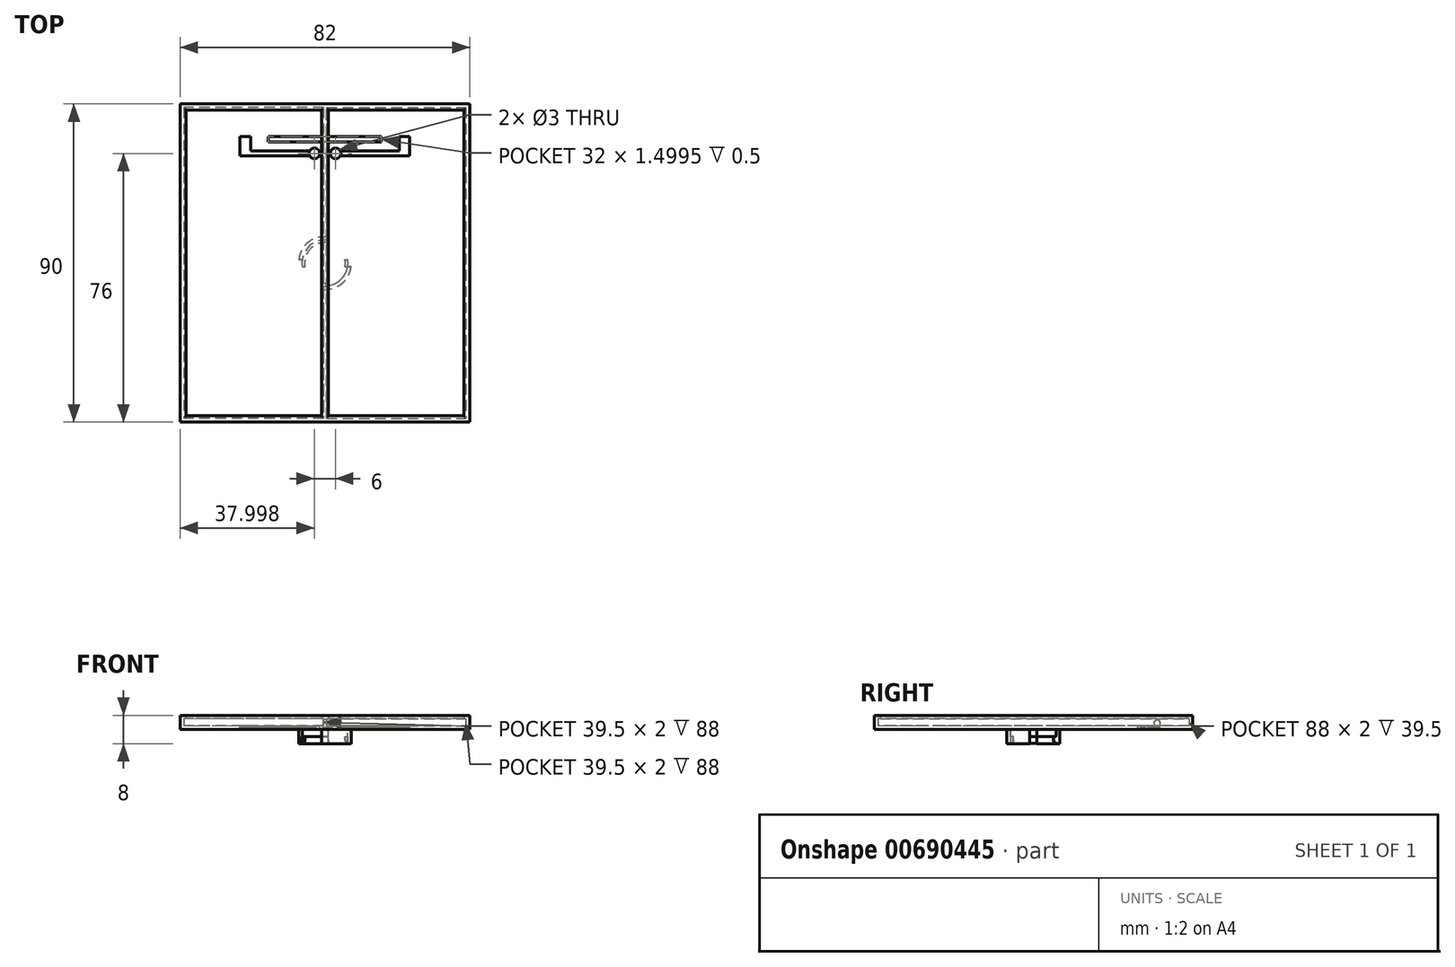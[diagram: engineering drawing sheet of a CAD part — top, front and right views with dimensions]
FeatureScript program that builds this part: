
annotation { "Feature Type Name" : "Feature", "Feature Type Description" : "" }
export const myFeature = defineFeature(function(context is Context, id is Id, definition is map)
    precondition{}
    {
        {
            var Q0;
            Q0=qCreatedBy(makeId("Top.planeOp"),FACE);
            var sketch = newSketch(context, id + "F0", { "sketchPlane" : qUnion([Q0])});
            skLineSegment(sketch, "E0.bottom", {"start": v(41, -45) * mm, "end": v(-41, -45) * mm});
            skLineSegment(sketch, "E0.top", {"start": v(41, 45) * mm, "end": v(-41, 45) * mm});
            skLineSegment(sketch, "E0.left", {"start": v(41, -45) * mm, "end": v(41, 45) * mm});
            skLineSegment(sketch, "E0.right", {"start": v(-41, -45) * mm, "end": v(-41, 45) * mm});
            skPoint(sketch, "E0.middle", {"position": v(0, 0) * mm});
            skPoint(sketch, "E1.startSnap0", {"position": v(0, 45) * mm});
            skPoint(sketch, "E1.endSnap0", {"position": v(0, -45) * mm});
            skLineSegment(sketch, "E2.top", {"start": v(1, 45) * mm, "end": v(0, 45) * mm});
            skLineSegment(sketch, "E2.left", {"start": v(1, -43.25) * mm, "end": v(1, 43.25) * mm});
            skLineSegment(sketch, "E2.right", {"start": v(-1, -43.25) * mm, "end": v(-1, 43.25) * mm});
            skLineSegment(sketch, "E3.bottom", {"start": v(39.27, -43.25) * mm, "end": v(1, -43.25) * mm});
            skLineSegment(sketch, "E3.top", {"start": v(39.27, 43.25) * mm, "end": v(1, 43.25) * mm});
            skLineSegment(sketch, "E3.left", {"start": v(39.27, -43.25) * mm, "end": v(39.27, 43.25) * mm});
            skLineSegment(sketch, "E3.right", {"start": v(-39.27, -43.25) * mm, "end": v(-39.27, 43.25) * mm});
            skLineSegment(sketch, "E4.trimOffspring", {"start": v(-1, -43.25) * mm, "end": v(-39.27, -43.25) * mm});
            skLineSegment(sketch, "E5.trimOffspring", {"start": v(-1, 43.25) * mm, "end": v(-39.27, 43.25) * mm});
            skPoint(sketch, "E6.orphan", {"position": v(-1, 45) * mm});
            skPoint(sketch, "E7.orphan", {"position": v(1, -45) * mm});
            skPoint(sketch, "E2.bottom.end.orphan", {"position": v(-1, -45) * mm});
            skLineSegment(sketch, "E8.bottom", {"start": v(-0.39, 44) * mm, "end": v(-39.89, 44) * mm});
            skLineSegment(sketch, "E8.top", {"start": v(-0.39, -44) * mm, "end": v(-39.89, -44) * mm});
            skLineSegment(sketch, "E8.left", {"start": v(-0.39, 44) * mm, "end": v(-0.39, -44) * mm});
            skLineSegment(sketch, "E8.right", {"start": v(-39.89, 44) * mm, "end": v(-39.89, -44) * mm});
            skPoint(sketch, "E8.middle", {"position": v(-20.14, 0) * mm});
            skLineSegment(sketch, "E9", {"start": v(0, -54.1) * mm, "end": v(0, 63.67) * mm, "construction": true});
            skLineSegment(sketch, "E10.MirrorCS", {"start": v(0.39, -44) * mm, "end": v(39.89, -44) * mm});
            skLineSegment(sketch, "E11.MirrorCS", {"start": v(0.39, 44) * mm, "end": v(0.39, -44) * mm});
            skLineSegment(sketch, "E12.MirrorCS", {"start": v(0.39, 44) * mm, "end": v(39.89, 44) * mm});
            skLineSegment(sketch, "E13.MirrorCS", {"start": v(39.89, 44) * mm, "end": v(39.89, -44) * mm});
            skSolve(sketch);
        }
        {
            var Q0;
            Q0=makeQuery(id+"F0.imprint","IMPRINT",FACE,{"disambiguationData":[TD([[makeQuery(id+"F0.imprint","IMPRINT",EDGE,{"derivedFrom":sQuery(id+"F0.wireOp",EDGE,"E2.right")}),-1.0]])]});
            var Q1;
            Q1=makeQuery(id+"F0.imprint","IMPRINT",FACE,{"disambiguationData":[TD([[makeQuery(id+"F0.imprint","IMPRINT",EDGE,{"derivedFrom":sQuery(id+"F0.wireOp",EDGE,"E2.left")}),1.0]])]});
            var Q2;
            Q2=makeQuery(id+"F0.imprint","IMPRINT",FACE,{"disambiguationData":[TD([[makeQuery(id+"F0.imprint","IMPRINT",EDGE,{"derivedFrom":sQuery(id+"F0.wireOp",EDGE,"E0.bottom")}),-1.0]])]});
            extrude(context, id + "F1", {"entities" : qUnion([Q0, Q1, Q2]), "depth" : 3 * mm, "offsetDistance" : 25 * mm});
        }
        {
            var Q0;
            {var subQ5=sQuery(id+"F0.wireOp",EDGE,"E3.left");Q0=makeQuery(id+"F0.imprint","IMPRINT",FACE,{"disambiguationData":[TD([[makeQuery(id+"F0.imprint","IMPRINT",EDGE,{"derivedFrom":subQ5}),1.0]])]});}
            var Q1;
            {var subQ5=sQuery(id+"F0.wireOp",EDGE,"E3.right");Q1=makeQuery(id+"F0.imprint","IMPRINT",FACE,{"disambiguationData":[TD([[makeQuery(id+"F0.imprint","IMPRINT",EDGE,{"derivedFrom":subQ5}),-1.0]])]});}
            var Q2;
            {var subQ5=sQuery(id+"F0.wireOp",EDGE,"E0.left");Q2=makeQuery(id+"F0.imprint","IMPRINT",FACE,{"disambiguationData":[TD([[makeQuery(id+"F0.imprint","IMPRINT",EDGE,{"derivedFrom":subQ5}),1.0]])]});}
            var Q3;
            {var subQ0=sQuery(id+"F0.wireOp",EDGE,"E0.right");Q3=makeQuery(id+"F0.imprint","IMPRINT",FACE,{"disambiguationData":[TD([[makeQuery(id+"F0.imprint","IMPRINT",EDGE,{"derivedFrom":subQ0}),-1.0]])]});}
            var Q4;
            {var subQ0=sQuery(id+"F0.wireOp",EDGE,"E3.bottom");var subQ1=sQuery(id+"F0.wireOp",EDGE,"E2.left");var subQ2=makeQuery(id+"F0.imprint","INTERSECT",VERTEX,{"derivedFrom":[subQ1,subQ0]});Q4=makeQuery(id+"F0.imprint","IMPRINT",FACE,{"disambiguationData":[TD([[makeQuery(id+"F0.imprint","IMPRINT",EDGE,{"disambiguationData":[TD([[subQ2,-1.0]])],"derivedFrom":subQ1}),1.0]])]});}
            var Q5;
            {var subQ0=sQuery(id+"F0.wireOp",EDGE,"E2.top");Q5=makeQuery(id+"F0.imprint","IMPRINT",FACE,{"disambiguationData":[TD([[makeQuery(id+"F0.imprint","IMPRINT",EDGE,{"derivedFrom":subQ0}),1.0]])]});}
            var Q6;
            {var subQ0=sQuery(id+"F0.wireOp",EDGE,"E2.bottom");Q6=makeQuery(id+"F0.imprint","IMPRINT",FACE,{"disambiguationData":[TD([[makeQuery(id+"F0.imprint","IMPRINT",EDGE,{"derivedFrom":subQ0}),-1.0]])]});}
            var Q7;
            Q7=makeQuery(id+"F0.imprint","IMPRINT",FACE,{"disambiguationData":[TD([[makeQuery(id+"F0.imprint","IMPRINT",EDGE,{"derivedFrom":sQuery(id+"F0.wireOp",EDGE,"E2.right")}),-1.0]])]});
            extrude(context, id + "F2", {"entities" : qUnion([Q0, Q1, Q2, Q3, Q4, Q5, Q6, Q7]), "operationType" : NewBodyOperationType.ADD, "oppositeDirection" : true, "depth" : 1 * mm, "offsetDistance" : 25 * mm});
        }
        {
            var Q0;
            Q0=makeQuery(id+"F0.imprint","IMPRINT",FACE,{"disambiguationData":[TD([[makeQuery(id+"F0.imprint","IMPRINT",EDGE,{"derivedFrom":sQuery(id+"F0.wireOp",EDGE,"E2.right")}),-1.0]])]});
            var Q1;
            Q1=makeQuery(id+"F0.imprint","IMPRINT",FACE,{"disambiguationData":[TD([[makeQuery(id+"F0.imprint","IMPRINT",EDGE,{"derivedFrom":sQuery(id+"F0.wireOp",EDGE,"E2.left")}),1.0]])]});
            extrude(context, id + "F3", {"entities" : qUnion([Q0, Q1]), "operationType" : NewBodyOperationType.REMOVE, "depth" : 2 * mm, "offsetDistance" : 25 * mm});
        }
        {
            var Q0;
            Q0=makeQuery(id+"F3.boolean.opBoolean","COPY",EDGE,{"derivedFrom":makeQuery(id+"F3.opExtrude","CAP_EDGE",EDGE,{"disambiguationData":[OSD([sQuery(id+"F0.wireOp",EDGE,"E3.left")])],"isStart":false})});
            var Q1;
            Q1=makeQuery(id+"F1.opExtrude","CAP_EDGE",EDGE,{"disambiguationData":[OSD([sQuery(id+"F0.wireOp",EDGE,"E3.left")])],"isStart":false});
            var Q2;
            Q2=makeQuery(id+"F3.boolean.opBoolean","COPY",EDGE,{"derivedFrom":makeQuery(id+"F3.opExtrude","CAP_EDGE",EDGE,{"disambiguationData":[OSD([sQuery(id+"F0.wireOp",EDGE,"E2.right")])],"isStart":false})});
            var Q3;
            Q3=makeQuery(id+"F1.opExtrude","CAP_EDGE",EDGE,{"disambiguationData":[OSD([sQuery(id+"F0.wireOp",EDGE,"E2.right")])],"isStart":false});
            var Q4;
            Q4=makeQuery(id+"F1.opExtrude","CAP_EDGE",EDGE,{"disambiguationData":[OSD([sQuery(id+"F0.wireOp",EDGE,"E4.trimOffspring")])],"isStart":false});
            var Q5;
            Q5=makeQuery(id+"F3.boolean.opBoolean","COPY",EDGE,{"derivedFrom":makeQuery(id+"F3.opExtrude","CAP_EDGE",EDGE,{"disambiguationData":[OSD([sQuery(id+"F0.wireOp",EDGE,"E4.trimOffspring")])],"isStart":false})});
            var Q6;
            Q6=makeQuery(id+"F3.boolean.opBoolean","COPY",EDGE,{"derivedFrom":makeQuery(id+"F3.opExtrude","CAP_EDGE",EDGE,{"disambiguationData":[OSD([sQuery(id+"F0.wireOp",EDGE,"E3.bottom")])],"isStart":false})});
            var Q7;
            Q7=makeQuery(id+"F1.opExtrude","CAP_EDGE",EDGE,{"disambiguationData":[OSD([sQuery(id+"F0.wireOp",EDGE,"E3.bottom")])],"isStart":false});
            var Q8;
            Q8=makeQuery(id+"F1.opExtrude","CAP_EDGE",EDGE,{"disambiguationData":[OSD([sQuery(id+"F0.wireOp",EDGE,"E2.left")])],"isStart":false});
            var Q9;
            Q9=makeQuery(id+"F3.boolean.opBoolean","COPY",EDGE,{"derivedFrom":makeQuery(id+"F3.opExtrude","CAP_EDGE",EDGE,{"disambiguationData":[OSD([sQuery(id+"F0.wireOp",EDGE,"E2.left")])],"isStart":false})});
            var Q10;
            Q10=makeQuery(id+"F1.opExtrude","CAP_EDGE",EDGE,{"disambiguationData":[OSD([sQuery(id+"F0.wireOp",EDGE,"E3.right")])],"isStart":false});
            var Q11;
            Q11=makeQuery(id+"F3.boolean.opBoolean","COPY",EDGE,{"derivedFrom":makeQuery(id+"F3.opExtrude","CAP_EDGE",EDGE,{"disambiguationData":[OSD([sQuery(id+"F0.wireOp",EDGE,"E3.right")])],"isStart":false})});
            var Q12;
            Q12=makeQuery(id+"F1.opExtrude","CAP_EDGE",EDGE,{"disambiguationData":[OSD([sQuery(id+"F0.wireOp",EDGE,"E5.trimOffspring")])],"isStart":false});
            var Q13;
            Q13=makeQuery(id+"F3.boolean.opBoolean","COPY",EDGE,{"derivedFrom":makeQuery(id+"F3.opExtrude","CAP_EDGE",EDGE,{"disambiguationData":[OSD([sQuery(id+"F0.wireOp",EDGE,"E5.trimOffspring")])],"isStart":false})});
            var Q14;
            Q14=makeQuery(id+"F3.boolean.opBoolean","COPY",EDGE,{"derivedFrom":makeQuery(id+"F3.opExtrude","CAP_EDGE",EDGE,{"disambiguationData":[OSD([sQuery(id+"F0.wireOp",EDGE,"E3.top")])],"isStart":false})});
            var Q15;
            Q15=makeQuery(id+"F1.opExtrude","CAP_EDGE",EDGE,{"disambiguationData":[OSD([sQuery(id+"F0.wireOp",EDGE,"E3.top")])],"isStart":false});
            fillet(context, id + "F4", {"entities" : qUnion([Q0, Q1, Q2, Q3, Q4, Q5, Q6, Q7, Q8, Q9, Q10, Q11, Q12, Q13, Q14, Q15]), "radius" : 0.25 * mm, "tangentPropagation" : true, "allowEdgeOverflow" : false});
        }
        {
            var Q0;
            Q0=makeQuery(id+"F3.boolean.opBoolean","COPY",FACE,{"derivedFrom":makeQuery(id+"F3.opExtrude","SWEPT_FACE",FACE,{"disambiguationData":[OSD([sQuery(id+"F0.wireOp",EDGE,"E8.left")])]})});
            var sketch = newSketch(context, id + "F5", { "sketchPlane" : qUnion([Q0])});
            skLineSegment(sketch, "E14", {"start": v(-44, 1) * mm, "end": v(-35, 1) * mm});
            skArc(sketch, "E15", {"start": v(-34.25, 0.97) * mm, "mid": v(-34.99, 1.75) * mm, "end": v(-35.75, 1) * mm});
            skLineSegment(sketch, "E16", {"start": v(-35.75, 1) * mm, "end": v(-35.75, 0) * mm});
            skLineSegment(sketch, "E17", {"start": v(-35.75, 0) * mm, "end": v(-34.25, 0) * mm});
            skLineSegment(sketch, "E18", {"start": v(-34.25, 0) * mm, "end": v(-34.25, 0.97) * mm});
            skSolve(sketch);
        }
        {
            var Q0;
            Q0=makeQuery(id+"F5.imprint","IMPRINT",FACE,{"disambiguationData":[TD([[makeQuery(id+"F5.imprint","IMPRINT",EDGE,{"derivedFrom":sQuery(id+"F5.wireOp",EDGE,"E15")}),1.0]])]});
            extrude(context, id + "F6", {"entities" : qUnion([Q0]), "operationType" : NewBodyOperationType.REMOVE, "oppositeDirection" : true, "depth" : 0.77 * mm, "offsetDistance" : 25 * mm});
        }
        {
            var Q0;
            {var subQ0=sQuery(id+"F0.wireOp",EDGE,"E5.trimOffspring");var subQ1=sQuery(id+"F0.wireOp",EDGE,"E4.trimOffspring");var subQ2=sQuery(id+"F0.wireOp",EDGE,"E3.right");var subQ3=sQuery(id+"F0.wireOp",EDGE,"E2.right");var subQ4=makeQuery(id+"F2.opExtrude","CAP_FACE",FACE,{"disambiguationData":[OSD([sQuery(id+"F0.wireOp",EDGE,"E0.bottom"),sQuery(id+"F0.wireOp",EDGE,"E0.top"),sQuery(id+"F0.wireOp",EDGE,"E0.left"),sQuery(id+"F0.wireOp",EDGE,"E0.right"),sQuery(id+"F0.wireOp",EDGE,"E2.top")])],"isStart":true});var subQ5=sQuery(id+"F0.wireOp",EDGE,"E3.left");var subQ6=sQuery(id+"F0.wireOp",EDGE,"E3.top");var subQ7=sQuery(id+"F0.wireOp",EDGE,"E3.bottom");var subQ8=sQuery(id+"F0.wireOp",EDGE,"E2.left");Q0=makeQuery(id+"F6.boolean.opBoolean","MERGE",FACE,{"derivedFrom":[makeQuery(id+"F3.boolean.opBoolean","MERGE",FACE,{"derivedFrom":[makeQuery(id+"F2.boolean.opBoolean","SPLIT",FACE,{"disambiguationData":[TD([makeQuery(id+"F1.opExtrude","SWEPT_FACE",FACE,{"disambiguationData":[OSD([subQ8])]})])],"derivedFrom":subQ4}),makeQuery(id+"F3.opExtrude","CAP_FACE",FACE,{"disambiguationData":[OSD([subQ8,subQ7,subQ6,subQ5,sQuery(id+"F0.wireOp",EDGE,"E10.MirrorCS"),sQuery(id+"F0.wireOp",EDGE,"E11.MirrorCS"),sQuery(id+"F0.wireOp",EDGE,"E12.MirrorCS"),sQuery(id+"F0.wireOp",EDGE,"E13.MirrorCS")])],"isStart":true})]}),makeQuery(id+"F3.boolean.opBoolean","MERGE",FACE,{"derivedFrom":[makeQuery(id+"F2.boolean.opBoolean","SPLIT",FACE,{"disambiguationData":[TD([makeQuery(id+"F1.opExtrude","SWEPT_FACE",FACE,{"disambiguationData":[OSD([subQ3])]})])],"derivedFrom":subQ4}),makeQuery(id+"F3.opExtrude","CAP_FACE",FACE,{"disambiguationData":[OSD([subQ3,subQ2,subQ1,subQ0,sQuery(id+"F0.wireOp",EDGE,"E8.bottom"),sQuery(id+"F0.wireOp",EDGE,"E8.top"),sQuery(id+"F0.wireOp",EDGE,"E8.left"),sQuery(id+"F0.wireOp",EDGE,"E8.right")])],"isStart":true})]}),makeQuery(id+"F6.opExtrude","SWEPT_FACE",FACE,{"disambiguationData":[OSD([sQuery(id+"F5.wireOp",EDGE,"E17")])]})]});}
            var sketch = newSketch(context, id + "F7", { "sketchPlane" : qUnion([Q0])});
            skLineSegment(sketch, "E19", {"start": v(0, 35.75) * mm, "end": v(0, 34.25) * mm});
            skLineSegment(sketch, "E20.bottom", {"start": v(16, 34.25) * mm, "end": v(-16, 34.25) * mm});
            skLineSegment(sketch, "E20.top", {"start": v(16, 35.75) * mm, "end": v(-16, 35.75) * mm});
            skLineSegment(sketch, "E20.left", {"start": v(16, 34.25) * mm, "end": v(16, 35.75) * mm});
            skLineSegment(sketch, "E20.right", {"start": v(-16, 34.25) * mm, "end": v(-16, 35.75) * mm});
            skPoint(sketch, "E20.middle", {"position": v(0, 35) * mm});
            skLineSegment(sketch, "E21", {"start": v(0, 35) * mm, "end": v(-22.5, 35) * mm});
            skLineSegment(sketch, "E22", {"start": v(0, 35) * mm, "end": v(22.5, 35) * mm});
            skLineSegment(sketch, "E23.top", {"start": v(-21, 35.75) * mm, "end": v(-24, 35.75) * mm});
            skPoint(sketch, "E23.middle", {"position": v(-22.5, 35) * mm});
            skLineSegment(sketch, "E24.top", {"start": v(24, 35.75) * mm, "end": v(21, 35.75) * mm});
            skPoint(sketch, "E24.middle", {"position": v(22.5, 35) * mm});
            skLineSegment(sketch, "E25.top", {"start": v(-24, 30.25) * mm, "end": v(-21, 30.25) * mm});
            skPoint(sketch, "E26.oppositeSnap0", {"position": v(-22.5, 30.25) * mm});
            skLineSegment(sketch, "E26.top", {"start": v(24, 30.25) * mm, "end": v(21, 30.25) * mm});
            skLineSegment(sketch, "E27", {"start": v(-24, 35.75) * mm, "end": v(-24, 30.25) * mm});
            skLineSegment(sketch, "E28", {"start": v(-21, 35.75) * mm, "end": v(-21, 31.75) * mm});
            skLineSegment(sketch, "E29", {"start": v(21, 35.75) * mm, "end": v(21, 31.75) * mm});
            skLineSegment(sketch, "E30", {"start": v(24, 35.75) * mm, "end": v(24, 30.25) * mm});
            skLineSegment(sketch, "E31.bottom", {"start": v(-21, 30.25) * mm, "end": v(-4.3, 30.25) * mm});
            skLineSegment(sketch, "E31.top", {"start": v(-21, 31.75) * mm, "end": v(-4.3, 31.75) * mm});
            skLineSegment(sketch, "E32.bottom", {"start": v(21, 30.25) * mm, "end": v(4.3, 30.25) * mm});
            skLineSegment(sketch, "E32.top", {"start": v(21, 31.75) * mm, "end": v(4.3, 31.75) * mm});
            skLineSegment(sketch, "E33", {"start": v(-1.5, 31) * mm, "end": v(-3, 31) * mm});
            skLineSegment(sketch, "E34", {"start": v(1.5, 31) * mm, "end": v(3, 31) * mm});
            skCircle(sketch, "E35", {"center": v(-3, 31) * mm, "radius": 1.5 * mm});
            skCircle(sketch, "E36", {"center": v(3, 31) * mm, "radius": 1.5 * mm});
            skPoint(sketch, "E37.trimOffspring.end.orphan", {"position": v(-1.5, 31.75) * mm});
            skPoint(sketch, "E31.right.start.orphan", {"position": v(-1.5, 30.25) * mm});
            skPoint(sketch, "E38.orphan", {"position": v(1.5, 31.75) * mm});
            skPoint(sketch, "E39.trimOffspring.end.orphan", {"position": v(1.5, 30.25) * mm});
            skSolve(sketch);
        }
        {
            var Q0;
            {var subQ14=sQuery(id+"F7.wireOp",EDGE,"E19");Q0=makeQuery(id+"F7.imprint","IMPRINT",FACE,{"disambiguationData":[TD([[makeQuery(id+"F7.imprint","IMPRINT",EDGE,{"derivedFrom":subQ14}),-1.0]])]});}
            var Q1;
            {var subQ11=sQuery(id+"F7.wireOp",EDGE,"E19");Q1=makeQuery(id+"F7.imprint","IMPRINT",FACE,{"disambiguationData":[TD([[makeQuery(id+"F7.imprint","IMPRINT",EDGE,{"derivedFrom":subQ11}),1.0]])]});}
            extrude(context, id + "F8", {"entities" : qUnion([Q0, Q1]), "operationType" : NewBodyOperationType.REMOVE, "oppositeDirection" : true, "depth" : 0.5 * mm, "offsetDistance" : 25 * mm});
        }
        {
            var Q0;
            {var subQ4=sQuery(id+"F7.wireOp",EDGE,"E23.top");Q0=makeQuery(id+"F7.imprint","IMPRINT",FACE,{"disambiguationData":[TD([[makeQuery(id+"F7.imprint","IMPRINT",EDGE,{"derivedFrom":subQ4}),1.0]])]});}
            var Q1;
            {var subQ1=sQuery(id+"F7.wireOp",EDGE,"E24.top");Q1=makeQuery(id+"F7.imprint","IMPRINT",FACE,{"disambiguationData":[TD([[makeQuery(id+"F7.imprint","IMPRINT",EDGE,{"derivedFrom":subQ1}),1.0]])]});}
            extrude(context, id + "F9", {"entities" : qUnion([Q0, Q1]), "operationType" : NewBodyOperationType.REMOVE, "oppositeDirection" : true, "depth" : 0.5 * mm, "offsetDistance" : 25 * mm});
        }
        {
            var Q0;
            {var subQ0=sQuery(id+"F7.wireOp",EDGE,"E35");var subQ2=makeQuery(id+"F7.imprint","IMPRINT",VERTEX,{"derivedFrom":subQ0});Q0=makeQuery(id+"F7.imprint","IMPRINT",FACE,{"disambiguationData":[TD([[makeQuery(id+"F7.imprint","IMPRINT",EDGE,{"disambiguationData":[TD([[subQ2,-1.0]])],"derivedFrom":subQ0}),1.0]])]});}
            var Q1;
            {var subQ0=sQuery(id+"F7.wireOp",EDGE,"E36");var subQ2=makeQuery(id+"F7.imprint","IMPRINT",VERTEX,{"derivedFrom":subQ0});Q1=makeQuery(id+"F7.imprint","IMPRINT",FACE,{"disambiguationData":[TD([[makeQuery(id+"F7.imprint","IMPRINT",EDGE,{"disambiguationData":[TD([[subQ2,1.0]])],"derivedFrom":subQ0}),1.0]])]});}
            extrude(context, id + "F10", {"entities" : qUnion([Q0, Q1]), "operationType" : NewBodyOperationType.REMOVE, "oppositeDirection" : true, "depth" : 1 * mm, "offsetDistance" : 25 * mm});
        }
        {
            var Q0;
            Q0=makeQuery(id+"F2.opExtrude","CAP_FACE",FACE,{"disambiguationData":[OSD([sQuery(id+"F0.wireOp",EDGE,"E0.bottom"),sQuery(id+"F0.wireOp",EDGE,"E0.top"),sQuery(id+"F0.wireOp",EDGE,"E0.left"),sQuery(id+"F0.wireOp",EDGE,"E0.right"),sQuery(id+"F0.wireOp",EDGE,"E2.top")])],"isStart":false});
            var sketch = newSketch(context, id + "F11", { "sketchPlane" : qUnion([Q0])});
            skCircle(sketch, "E40", {"center": v(0, 0) * mm, "radius": 7.5 * mm});
            skCircle(sketch, "E41", {"center": v(0, 0) * mm, "radius": 6.5 * mm});
            skCircle(sketch, "E42", {"center": v(0, 0) * mm, "radius": 5.75 * mm});
            skLineSegment(sketch, "E43.bottom", {"start": v(10.78, -1) * mm, "end": v(-10.78, -1) * mm});
            skLineSegment(sketch, "E43.top", {"start": v(10.78, 1) * mm, "end": v(-10.78, 1) * mm});
            skLineSegment(sketch, "E43.left", {"start": v(10.78, -1) * mm, "end": v(10.78, 1) * mm});
            skLineSegment(sketch, "E43.right", {"start": v(-10.78, -1) * mm, "end": v(-10.78, 1) * mm});
            skLineSegment(sketch, "E44.bottom", {"start": v(-1, 9.3) * mm, "end": v(1, 9.3) * mm});
            skLineSegment(sketch, "E44.top", {"start": v(-1, -9.3) * mm, "end": v(1, -9.3) * mm});
            skLineSegment(sketch, "E44.left", {"start": v(-1, 9.3) * mm, "end": v(-1, -9.3) * mm});
            skLineSegment(sketch, "E44.right", {"start": v(1, 9.3) * mm, "end": v(1, -9.3) * mm});
            skSolve(sketch);
        }
        {
            var Q0;
            Q0=makeQuery(id+"F11.imprint","IMPRINT",FACE,{"disambiguationData":[TD([[makeQuery(id+"F11.imprint","IMPRINT",EDGE,{"derivedFrom":sQuery(id+"F11.wireOp",EDGE,"E41")}),1.0]])]});
            var Q1;
            Q1=makeQuery(id+"F11.imprint","IMPRINT",FACE,{"disambiguationData":[TD([[makeQuery(id+"F11.imprint","IMPRINT",EDGE,{"derivedFrom":sQuery(id+"F11.wireOp",EDGE,"E40")}),1.0]])]});
            extrude(context, id + "F12", {"entities" : qUnion([Q0, Q1]), "operationType" : NewBodyOperationType.ADD, "depth" : 4 * mm, "offsetDistance" : 25 * mm});
        }
        {
            var Q0;
            Q0=makeQuery(id+"F11.imprint","IMPRINT",FACE,{"disambiguationData":[TD([[makeQuery(id+"F11.imprint","IMPRINT",EDGE,{"derivedFrom":sQuery(id+"F11.wireOp",EDGE,"E41")}),1.0]])]});
            extrude(context, id + "F13", {"entities" : qUnion([Q0]), "operationType" : NewBodyOperationType.REMOVE, "depth" : 2 * mm, "offsetDistance" : 25 * mm});
        }
        {
            var Q0;
            Q0=makeQuery(id+"F12.opExtrude","CAP_EDGE",EDGE,{"disambiguationData":[OSD([sQuery(id+"F11.wireOp",EDGE,"E42")])],"isStart":false});
            var Q1;
            Q1=makeQuery(id+"F13.boolean.opBoolean","COPY",EDGE,{"derivedFrom":makeQuery(id+"F13.opExtrude","CAP_EDGE",EDGE,{"disambiguationData":[OSD([sQuery(id+"F11.wireOp",EDGE,"E42")])],"isStart":false})});
            fillet(context, id + "F14", {"entities" : qUnion([Q0, Q1]), "radius" : 1 * mm, "tangentPropagation" : true, "allowEdgeOverflow" : false});
        }
        {
            var Q0;
            {var subQ0=sQuery(id+"F11.wireOp",EDGE,"E43.top");var subQ1=sQuery(id+"F11.wireOp",EDGE,"E41");var subQ2=makeQuery(id+"F11.imprint","INTERSECT",VERTEX,{"disambiguationData":[OD(1.0)],"derivedFrom":[subQ1,subQ0]});Q0=makeQuery(id+"F11.imprint","IMPRINT",FACE,{"disambiguationData":[TD([[makeQuery(id+"F11.imprint","IMPRINT",EDGE,{"disambiguationData":[TD([[subQ2,-1.0]])],"derivedFrom":subQ1}),1.0]])]});}
            var Q1;
            {var subQ0=sQuery(id+"F11.wireOp",EDGE,"E43.top");var subQ1=sQuery(id+"F11.wireOp",EDGE,"E40");var subQ2=makeQuery(id+"F11.imprint","INTERSECT",VERTEX,{"disambiguationData":[OD(1.0)],"derivedFrom":[subQ1,subQ0]});Q1=makeQuery(id+"F11.imprint","IMPRINT",FACE,{"disambiguationData":[TD([[makeQuery(id+"F11.imprint","IMPRINT",EDGE,{"disambiguationData":[TD([[subQ2,-1.0]])],"derivedFrom":subQ1}),1.0]])]});}
            var Q2;
            {var subQ0=sQuery(id+"F11.wireOp",EDGE,"E44.right");var subQ1=sQuery(id+"F11.wireOp",EDGE,"E41");var subQ2=makeQuery(id+"F11.imprint","INTERSECT",VERTEX,{"disambiguationData":[OD(0.0)],"derivedFrom":[subQ1,subQ0]});Q2=makeQuery(id+"F11.imprint","IMPRINT",FACE,{"disambiguationData":[TD([[makeQuery(id+"F11.imprint","IMPRINT",EDGE,{"disambiguationData":[TD([[subQ2,-1.0]])],"derivedFrom":subQ1}),1.0]])]});}
            var Q3;
            {var subQ0=sQuery(id+"F11.wireOp",EDGE,"E44.right");var subQ1=sQuery(id+"F11.wireOp",EDGE,"E40");var subQ2=makeQuery(id+"F11.imprint","INTERSECT",VERTEX,{"disambiguationData":[OD(0.0)],"derivedFrom":[subQ1,subQ0]});Q3=makeQuery(id+"F11.imprint","IMPRINT",FACE,{"disambiguationData":[TD([[makeQuery(id+"F11.imprint","IMPRINT",EDGE,{"disambiguationData":[TD([[subQ2,-1.0]])],"derivedFrom":subQ1}),1.0]])]});}
            var Q4;
            {var subQ0=sQuery(id+"F11.wireOp",EDGE,"E43.top");var subQ1=sQuery(id+"F11.wireOp",EDGE,"E40");var subQ2=makeQuery(id+"F11.imprint","INTERSECT",VERTEX,{"disambiguationData":[OD(0.0)],"derivedFrom":[subQ1,subQ0]});Q4=makeQuery(id+"F11.imprint","IMPRINT",FACE,{"disambiguationData":[TD([[makeQuery(id+"F11.imprint","IMPRINT",EDGE,{"disambiguationData":[TD([[subQ2,1.0]])],"derivedFrom":subQ1}),1.0]])]});}
            var Q5;
            {var subQ0=sQuery(id+"F11.wireOp",EDGE,"E43.top");var subQ1=sQuery(id+"F11.wireOp",EDGE,"E41");var subQ2=makeQuery(id+"F11.imprint","INTERSECT",VERTEX,{"disambiguationData":[OD(0.0)],"derivedFrom":[subQ1,subQ0]});Q5=makeQuery(id+"F11.imprint","IMPRINT",FACE,{"disambiguationData":[TD([[makeQuery(id+"F11.imprint","IMPRINT",EDGE,{"disambiguationData":[TD([[subQ2,1.0]])],"derivedFrom":subQ1}),1.0]])]});}
            var Q6;
            {var subQ0=sQuery(id+"F11.wireOp",EDGE,"E44.left");var subQ1=sQuery(id+"F11.wireOp",EDGE,"E40");var subQ2=makeQuery(id+"F11.imprint","INTERSECT",VERTEX,{"disambiguationData":[OD(1.0)],"derivedFrom":[subQ1,subQ0]});Q6=makeQuery(id+"F11.imprint","IMPRINT",FACE,{"disambiguationData":[TD([[makeQuery(id+"F11.imprint","IMPRINT",EDGE,{"disambiguationData":[TD([[subQ2,-1.0]])],"derivedFrom":subQ1}),1.0]])]});}
            var Q7;
            {var subQ0=sQuery(id+"F11.wireOp",EDGE,"E44.left");var subQ1=sQuery(id+"F11.wireOp",EDGE,"E41");var subQ2=makeQuery(id+"F11.imprint","INTERSECT",VERTEX,{"disambiguationData":[OD(1.0)],"derivedFrom":[subQ1,subQ0]});Q7=makeQuery(id+"F11.imprint","IMPRINT",FACE,{"disambiguationData":[TD([[makeQuery(id+"F11.imprint","IMPRINT",EDGE,{"disambiguationData":[TD([[subQ2,-1.0]])],"derivedFrom":subQ1}),1.0]])]});}
            extrude(context, id + "F15", {"entities" : qUnion([Q0, Q1, Q2, Q3, Q4, Q5, Q6, Q7]), "operationType" : NewBodyOperationType.REMOVE, "depth" : 25 * mm, "offsetDistance" : 25 * mm});
        }
    });
